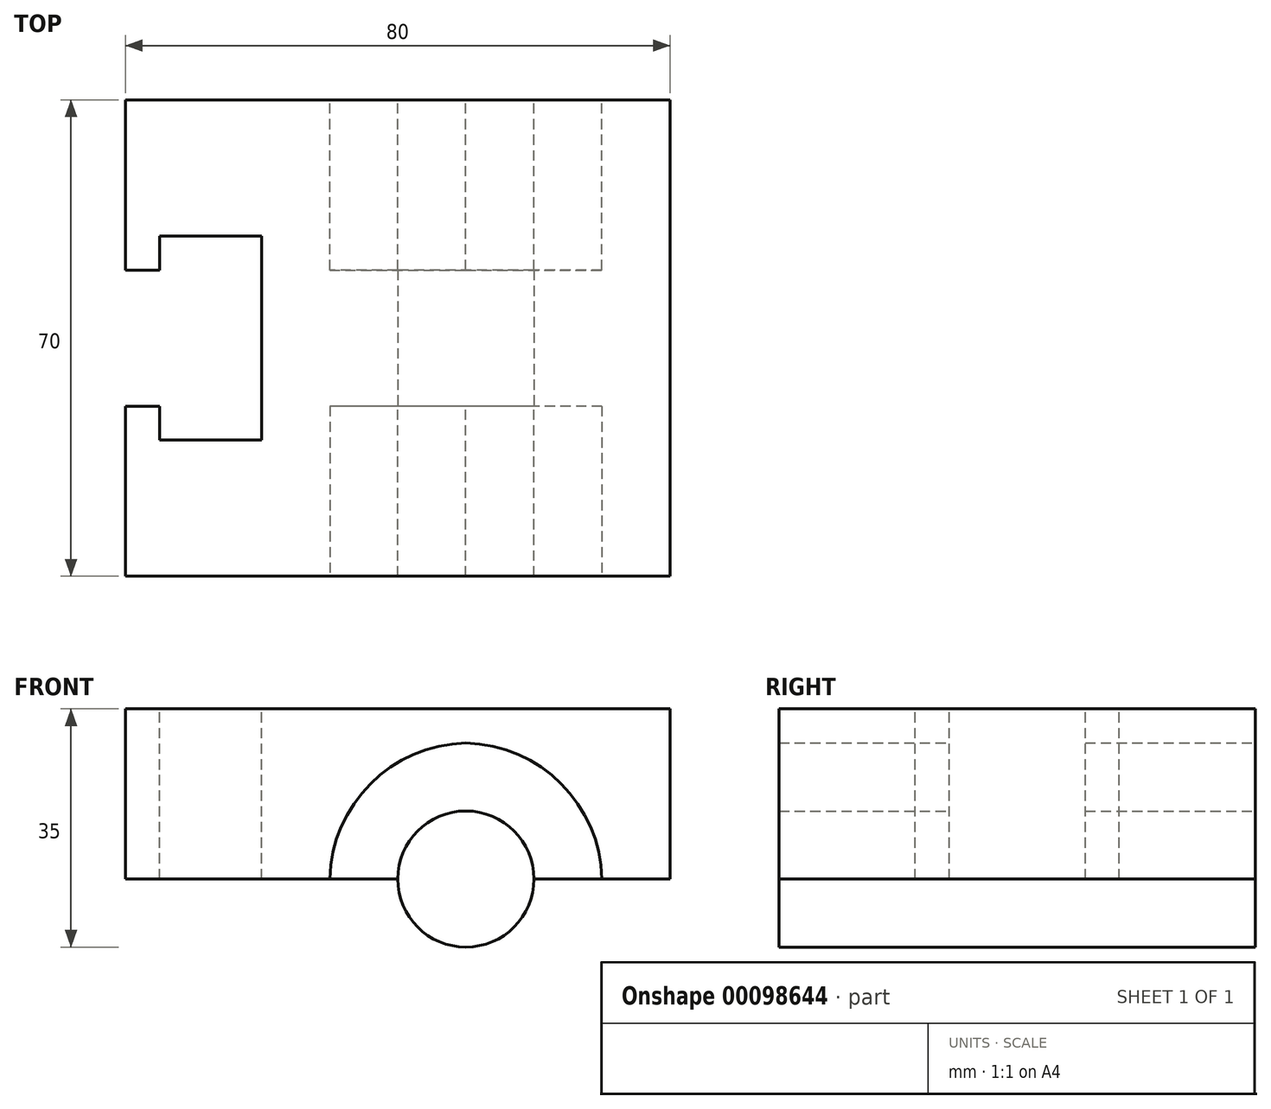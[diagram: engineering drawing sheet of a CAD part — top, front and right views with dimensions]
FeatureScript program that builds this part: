
annotation { "Feature Type Name" : "Feature", "Feature Type Description" : "" }
export const myFeature = defineFeature(function(context is Context, id is Id, definition is map)
    precondition{}
    {
        {
            var Q0;
            Q0=qCreatedBy(makeId("Right.planeOp"),FACE);
            var sketch = newSketch(context, id + "F0", { "sketchPlane" : qUnion([Q0])});
            skLineSegment(sketch, "E0.bottom", {"start": v(35, 12.5) * mm, "end": v(-35, 12.5) * mm});
            skLineSegment(sketch, "E0.top", {"start": v(35, -12.5) * mm, "end": v(-35, -12.5) * mm});
            skLineSegment(sketch, "E0.left", {"start": v(35, 12.5) * mm, "end": v(35, -12.5) * mm});
            skLineSegment(sketch, "E0.right", {"start": v(-35, 12.5) * mm, "end": v(-35, -12.5) * mm});
            skPoint(sketch, "E0.middle", {"position": v(0, 0) * mm});
            skSolve(sketch);
        }
        {
            var Q0;
            Q0=makeQuery(id+"F0.imprint","IMPRINT",FACE,{"disambiguationData":[TD([[makeQuery(id+"F0.imprint","IMPRINT",EDGE,{"derivedFrom":sQuery(id+"F0.wireOp",EDGE,"E0.bottom")}),1.0]])]});
            extrude(context, id + "F1", {"entities" : qUnion([Q0]), "depth" : 40 * mm, "hasSecondDirection" : true, "secondDirectionOppositeDirection" : true, "secondDirectionDepth" : 40 * mm});
        }
        {
            var Q0;
            Q0=makeQuery(id+"F1.opExtrude","SWEPT_FACE",FACE,{"disambiguationData":[OSD([sQuery(id+"F0.wireOp",EDGE,"E0.bottom")])]});
            var sketch = newSketch(context, id + "F2", { "sketchPlane" : qUnion([Q0])});
            skLineSegment(sketch, "E1", {"start": v(-40, 0) * mm, "end": v(-20, 0) * mm});
            skLineSegment(sketch, "E2", {"start": v(-20, 0) * mm, "end": v(-20, 15) * mm});
            skLineSegment(sketch, "E3", {"start": v(-20, 15) * mm, "end": v(-35, 15) * mm});
            skLineSegment(sketch, "E4", {"start": v(-35, 15) * mm, "end": v(-35, 10) * mm});
            skLineSegment(sketch, "E5", {"start": v(-35, 10) * mm, "end": v(-40, 10) * mm});
            skLineSegment(sketch, "E6", {"start": v(-40, 10) * mm, "end": v(-40, 0) * mm});
            skLineSegment(sketch, "E7.MirrorCS", {"start": v(-35, -10) * mm, "end": v(-40, -10) * mm});
            skLineSegment(sketch, "E8.MirrorCS", {"start": v(-35, -15) * mm, "end": v(-35, -10) * mm});
            skLineSegment(sketch, "E9.MirrorCS", {"start": v(-40, -10) * mm, "end": v(-40, 0) * mm});
            skLineSegment(sketch, "E10.MirrorCS", {"start": v(-20, -15) * mm, "end": v(-35, -15) * mm});
            skLineSegment(sketch, "E11.MirrorCS", {"start": v(-20, 0) * mm, "end": v(-20, -15) * mm});
            skSolve(sketch);
        }
        {
            var Q0;
            Q0=makeQuery(id+"F2.imprint","IMPRINT",FACE,{"disambiguationData":[TD([[makeQuery(id+"F2.imprint","IMPRINT",EDGE,{"derivedFrom":sQuery(id+"F2.wireOp",EDGE,"E1")}),1.0]])]});
            var Q1;
            Q1=makeQuery(id+"F2.imprint","IMPRINT",FACE,{"disambiguationData":[TD([[makeQuery(id+"F2.imprint","IMPRINT",EDGE,{"derivedFrom":sQuery(id+"F2.wireOp",EDGE,"E1")}),-1.0]])]});
            extrude(context, id + "F3", {"entities" : qUnion([Q0, Q1]), "operationType" : NewBodyOperationType.REMOVE, "oppositeDirection" : true, "depth" : 40 * mm});
        }
        {
            var Q0;
            Q0=makeQuery(id+"F1.opExtrude","SWEPT_FACE",FACE,{"disambiguationData":[OSD([sQuery(id+"F0.wireOp",EDGE,"E0.right")])]});
            var sketch = newSketch(context, id + "F4", { "sketchPlane" : qUnion([Q0])});
            skLineSegment(sketch, "E12.bottom", {"start": v(-10, -12.5) * mm, "end": v(30, -12.5) * mm});
            skLineSegment(sketch, "E12.top", {"start": v(-10, 7.5) * mm, "end": v(30, 7.5) * mm});
            skLineSegment(sketch, "E12.left", {"start": v(-10, -12.5) * mm, "end": v(-10, 7.5) * mm});
            skLineSegment(sketch, "E12.right", {"start": v(30, -12.5) * mm, "end": v(30, 7.5) * mm});
            skSolve(sketch);
        }
        {
            var Q0;
            Q0=makeQuery(id+"F4.imprint","IMPRINT",FACE,{"disambiguationData":[TD([[makeQuery(id+"F4.imprint","IMPRINT",EDGE,{"derivedFrom":sQuery(id+"F4.wireOp",EDGE,"E12.bottom")}),-1.0]])]});
            extrude(context, id + "F5", {"entities" : qUnion([Q0]), "operationType" : NewBodyOperationType.REMOVE, "oppositeDirection" : true, "depth" : 25 * mm});
        }
        {
            var Q0;
            Q0=makeQuery(id+"F5.boolean.opBoolean","COPY",FACE,{"derivedFrom":makeQuery(id+"F5.opExtrude","CAP_FACE",FACE,{"disambiguationData":[OSD([sQuery(id+"F4.wireOp",EDGE,"E12.bottom"),sQuery(id+"F4.wireOp",EDGE,"E12.top"),sQuery(id+"F4.wireOp",EDGE,"E12.left"),sQuery(id+"F4.wireOp",EDGE,"E12.right")])],"isStart":false})});
            var sketch = newSketch(context, id + "F6", { "sketchPlane" : qUnion([Q0])});
            skCircle(sketch, "E13", {"center": v(10, -12.5) * mm, "radius": 10 * mm});
            skSolve(sketch);
        }
        {
            var Q0;
            {var subQ0=sQuery(id+"F6.wireOp",EDGE,"E13");var subQ1=makeQuery(id+"F5.boolean.opBoolean","COPY",EDGE,{"derivedFrom":makeQuery(id+"F5.opExtrude","CAP_EDGE",EDGE,{"disambiguationData":[OSD([sQuery(id+"F4.wireOp",EDGE,"E12.bottom")])],"isStart":false})});var subQ2=makeQuery(id+"F6.imprint","INTERSECT",VERTEX,{"disambiguationData":[OD(0.0)],"derivedFrom":[subQ1,subQ0]});Q0=makeQuery(id+"F6.imprint","IMPRINT",FACE,{"disambiguationData":[TD([[makeQuery(id+"F6.imprint","IMPRINT",EDGE,{"disambiguationData":[TD([[subQ2,1.0]])],"derivedFrom":subQ0}),1.0]])]});}
            var Q1;
            {var subQ0=sQuery(id+"F6.wireOp",EDGE,"E13");var subQ1=makeQuery(id+"F5.boolean.opBoolean","COPY",EDGE,{"derivedFrom":makeQuery(id+"F5.opExtrude","CAP_EDGE",EDGE,{"disambiguationData":[OSD([sQuery(id+"F4.wireOp",EDGE,"E12.bottom")])],"isStart":false})});var subQ2=makeQuery(id+"F6.imprint","INTERSECT",VERTEX,{"disambiguationData":[OD(0.0)],"derivedFrom":[subQ1,subQ0]});Q1=makeQuery(id+"F6.imprint","IMPRINT",FACE,{"disambiguationData":[TD([[makeQuery(id+"F6.imprint","IMPRINT",EDGE,{"disambiguationData":[TD([[subQ2,-1.0]])],"derivedFrom":subQ0}),1.0]])]});}
            extrude(context, id + "F7", {"entities" : qUnion([Q0, Q1]), "operationType" : NewBodyOperationType.ADD, "depth" : 25 * mm});
        }
        {
            var Q0;
            Q0=makeQuery(id+"F1.opExtrude","SWEPT_FACE",FACE,{"disambiguationData":[OSD([sQuery(id+"F0.wireOp",EDGE,"E0.left")])]});
            var sketch = newSketch(context, id + "F8", { "sketchPlane" : qUnion([Q0])});
            skLineSegment(sketch, "E14.bottom", {"start": v(40, 12.5) * mm, "end": v(-40, 12.5) * mm});
            skLineSegment(sketch, "E14.top", {"start": v(40, -12.5) * mm, "end": v(-40, -12.5) * mm});
            skLineSegment(sketch, "E14.left", {"start": v(40, 12.5) * mm, "end": v(40, -12.5) * mm});
            skLineSegment(sketch, "E14.right", {"start": v(-40, 12.5) * mm, "end": v(-40, -12.5) * mm});
            skSolve(sketch);
        }
        {
            var Q0;
            Q0=makeQuery(id+"F8.imprint","IMPRINT",FACE,{"disambiguationData":[TD([[makeQuery(id+"F8.imprint","IMPRINT",EDGE,{"derivedFrom":sQuery(id+"F8.wireOp",EDGE,"E14.bottom")}),-1.0]])]});
            extrude(context, id + "F9", {"entities" : qUnion([Q0]), "operationType" : NewBodyOperationType.REMOVE, "oppositeDirection" : true, "depth" : 35 * mm});
        }
        {
            var Q0;
            Q0=makeQuery(id+"F1.opExtrude","SWEPT_BODY",BODY,{"disambiguationData":[OSD([sQuery(id+"F0.wireOp",EDGE,"E0.bottom"),sQuery(id+"F0.wireOp",EDGE,"E0.top"),sQuery(id+"F0.wireOp",EDGE,"E0.left"),sQuery(id+"F0.wireOp",EDGE,"E0.right")])]});
            var Q1;
            Q1=qCreatedBy(makeId("Front.planeOp"),FACE);
            mirror(context, id + "F10", {"operationType" : NewBodyOperationType.ADD, "entities" : qUnion([Q0]), "mirrorPlane" : qUnion([Q1])});
        }
        {
            var Q0;
            Q0=makeQuery(id+"F7.opExtrude","CAP_FACE",FACE,{"disambiguationData":[OSD([sQuery(id+"F6.wireOp",EDGE,"E13")])],"isStart":true});
            extrude(context, id + "F11", {"entities" : qUnion([Q0]), "operationType" : NewBodyOperationType.ADD, "depth" : 25 * mm});
        }
        {
            var Q0;
            Q0=makeQuery(id+"F10.opPattern","COPY",EDGE,{"derivedFrom":makeQuery(id+"F5.boolean.opBoolean","COPY",EDGE,{"derivedFrom":makeQuery(id+"F5.opExtrude","SWEPT_EDGE",EDGE,{"disambiguationData":[OSD([sQuery(id+"F4.wireOp",EDGE,"E12.top"),sQuery(id+"F4.wireOp",EDGE,"E12.right")])]})}),"instanceName":"1"});
            var Q1;
            Q1=makeQuery(id+"F10.opPattern","COPY",EDGE,{"derivedFrom":makeQuery(id+"F5.boolean.opBoolean","COPY",EDGE,{"derivedFrom":makeQuery(id+"F5.opExtrude","SWEPT_EDGE",EDGE,{"disambiguationData":[OSD([sQuery(id+"F4.wireOp",EDGE,"E12.top"),sQuery(id+"F4.wireOp",EDGE,"E12.left")])]})}),"instanceName":"1"});
            var Q2;
            Q2=makeQuery(id+"F5.boolean.opBoolean","COPY",EDGE,{"derivedFrom":makeQuery(id+"F5.opExtrude","SWEPT_EDGE",EDGE,{"disambiguationData":[OSD([sQuery(id+"F4.wireOp",EDGE,"E12.top"),sQuery(id+"F4.wireOp",EDGE,"E12.right")])]})});
            var Q3;
            Q3=makeQuery(id+"F5.boolean.opBoolean","COPY",EDGE,{"derivedFrom":makeQuery(id+"F5.opExtrude","SWEPT_EDGE",EDGE,{"disambiguationData":[OSD([sQuery(id+"F4.wireOp",EDGE,"E12.top"),sQuery(id+"F4.wireOp",EDGE,"E12.left")])]})});
            fillet(context, id + "F12", {"entities" : qUnion([Q0, Q1, Q2, Q3]), "radius" : 20.5 * mm, "tangentPropagation" : true, "allowEdgeOverflow" : false});
        }
    });
